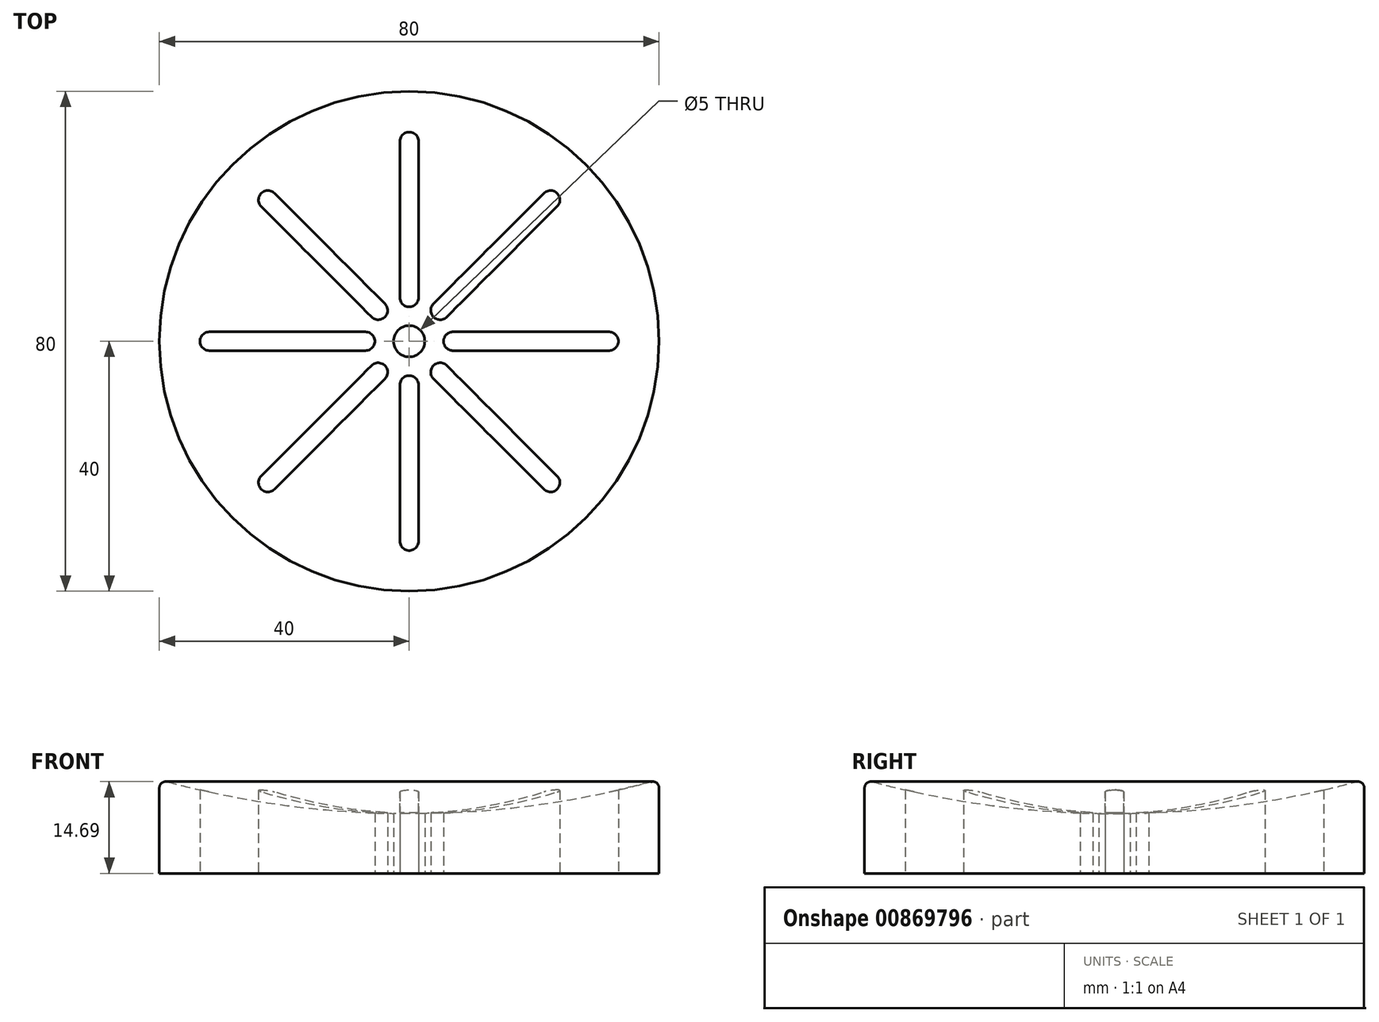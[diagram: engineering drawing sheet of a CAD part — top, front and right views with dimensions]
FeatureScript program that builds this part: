
annotation { "Feature Type Name" : "Feature", "Feature Type Description" : "" }
export const myFeature = defineFeature(function(context is Context, id is Id, definition is map)
    precondition{}
    {
        {
            var Q0;
            Q0=qCreatedBy(makeId("Top.planeOp"),FACE);
            var sketch = newSketch(context, id + "F0", { "sketchPlane" : qUnion([Q0])});
            skCircle(sketch, "E0", {"center": v(0, 0) * mm, "radius": 40 * mm});
            skSolve(sketch);
        }
        {
            var Q0;
            Q0=makeQuery(id+"F0.imprint","IMPRINT",FACE,{"disambiguationData":[TD([[makeQuery(id+"F0.imprint","IMPRINT",EDGE,{"derivedFrom":sQuery(id+"F0.wireOp",EDGE,"E0")}),1.0]])]});
            extrude(context, id + "F1", {"entities" : qUnion([Q0]), "depth" : 15 * mm, "offsetDistance" : 25 * mm});
        }
        {
            var Q0;
            Q0=qCreatedBy(makeId("Front.planeOp"),FACE);
            var sketch = newSketch(context, id + "F2", { "sketchPlane" : qUnion([Q0])});
            skArc(sketch, "E1", {"start": v(0, 9.57) * mm, "mid": v(20.18, 10.93) * mm, "end": v(40, 15) * mm});
            skLineSegment(sketch, "E2.0.0", {"start": v(0, 15) * mm, "end": v(40, 15) * mm});
            skLineSegment(sketch, "E3", {"start": v(0, 15) * mm, "end": v(0, 9.57) * mm});
            skPoint(sketch, "E4.orphan", {"position": v(-40, 15) * mm});
            skSolve(sketch);
        }
        {
            var Q0;
            Q0 = qSketchRegion(id + "F2", true);
            var Q1;
            Q1=sQuery(id+"F2.wireOp",EDGE,"E3");
            revolve(context, id + "F3", {"operationType" : NewBodyOperationType.REMOVE, "surfaceOperationType" : NewSurfaceOperationType.NEW, "entities" : qUnion([Q0]), "axis" : qUnion([Q1]), "revolveType" : RevolveType.FULL, "oppositeDirection" : true});
        }
        {
            var Q0;
            Q0=makeQuery(id+"F3.boolean.opBoolean","MERGE",EDGE,{"derivedFrom":[makeQuery(id+"F1.opExtrude","CAP_EDGE",EDGE,{"disambiguationData":[OSD([sQuery(id+"F0.wireOp",EDGE,"E0")])],"isStart":false}),makeQuery(id+"F3.opRevolve","SWEPT_EDGE",EDGE,{"disambiguationData":[OSD([sQuery(id+"F2.wireOp",EDGE,"E1"),sQuery(id+"F2.wireOp",EDGE,"E2.0.0")])]})]});
            fillet(context, id + "F4", {"entities" : qUnion([Q0]), "radius" : 1 * mm, "tangentPropagation" : true, "allowEdgeOverflow" : false});
        }
        {
            var Q0;
            Q0=qCreatedBy(makeId("Top.planeOp"),FACE);
            var sketch = newSketch(context, id + "F5", { "sketchPlane" : qUnion([Q0])});
            skCircle(sketch, "E5", {"center": v(0, 0) * mm, "radius": 2.5 * mm});
            skArc(sketch, "E6", {"start": v(-1.5, 7) * mm, "mid": v(0, 5.5) * mm, "end": v(1.5, 7) * mm});
            skArc(sketch, "E7", {"start": v(1.5, 32) * mm, "mid": v(0, 33.5) * mm, "end": v(-1.5, 32) * mm});
            skLineSegment(sketch, "E8", {"start": v(-1.5, 32) * mm, "end": v(-1.5, 7) * mm});
            skLineSegment(sketch, "E9", {"start": v(1.5, 32) * mm, "end": v(1.5, 7) * mm});
            skArc(sketch, "E10.1.0", {"start": v(-21.57, 23.69) * mm, "mid": v(-23.69, 23.69) * mm, "end": v(-23.69, 21.57) * mm});
            skLineSegment(sketch, "E10.1.1", {"start": v(-23.69, 21.57) * mm, "end": v(-6.01, 3.89) * mm});
            skLineSegment(sketch, "E10.1.2", {"start": v(-21.57, 23.69) * mm, "end": v(-3.89, 6.01) * mm});
            skArc(sketch, "E10.1.3", {"start": v(-6.01, 3.89) * mm, "mid": v(-3.89, 3.89) * mm, "end": v(-3.89, 6.01) * mm});
            skArc(sketch, "E10.2.0", {"start": v(-32, 1.5) * mm, "mid": v(-33.5, 0) * mm, "end": v(-32, -1.5) * mm});
            skLineSegment(sketch, "E10.2.1", {"start": v(-32, -1.5) * mm, "end": v(-7, -1.5) * mm});
            skLineSegment(sketch, "E10.2.2", {"start": v(-32, 1.5) * mm, "end": v(-7, 1.5) * mm});
            skArc(sketch, "E10.2.3", {"start": v(-7, -1.5) * mm, "mid": v(-5.5, 0) * mm, "end": v(-7, 1.5) * mm});
            skArc(sketch, "E10.3.0", {"start": v(-23.69, -21.57) * mm, "mid": v(-23.69, -23.69) * mm, "end": v(-21.57, -23.69) * mm});
            skLineSegment(sketch, "E10.3.1", {"start": v(-21.57, -23.69) * mm, "end": v(-3.89, -6.01) * mm});
            skLineSegment(sketch, "E10.3.2", {"start": v(-23.69, -21.57) * mm, "end": v(-6.01, -3.89) * mm});
            skArc(sketch, "E10.3.3", {"start": v(-3.89, -6.01) * mm, "mid": v(-3.89, -3.89) * mm, "end": v(-6.01, -3.89) * mm});
            skArc(sketch, "E10.4.0", {"start": v(-1.5, -32) * mm, "mid": v(0, -33.5) * mm, "end": v(1.5, -32) * mm});
            skLineSegment(sketch, "E10.4.1", {"start": v(1.5, -32) * mm, "end": v(1.5, -7) * mm});
            skLineSegment(sketch, "E10.4.2", {"start": v(-1.5, -32) * mm, "end": v(-1.5, -7) * mm});
            skArc(sketch, "E10.4.3", {"start": v(1.5, -7) * mm, "mid": v(0, -5.5) * mm, "end": v(-1.5, -7) * mm});
            skArc(sketch, "E10.5.0", {"start": v(21.57, -23.69) * mm, "mid": v(23.69, -23.69) * mm, "end": v(23.69, -21.57) * mm});
            skLineSegment(sketch, "E10.5.1", {"start": v(23.69, -21.57) * mm, "end": v(6.01, -3.89) * mm});
            skLineSegment(sketch, "E10.5.2", {"start": v(21.57, -23.69) * mm, "end": v(3.89, -6.01) * mm});
            skArc(sketch, "E10.5.3", {"start": v(6.01, -3.89) * mm, "mid": v(3.89, -3.89) * mm, "end": v(3.89, -6.01) * mm});
            skArc(sketch, "E10.6.0", {"start": v(32, -1.5) * mm, "mid": v(33.5, 0) * mm, "end": v(32, 1.5) * mm});
            skLineSegment(sketch, "E10.6.1", {"start": v(32, 1.5) * mm, "end": v(7, 1.5) * mm});
            skLineSegment(sketch, "E10.6.2", {"start": v(32, -1.5) * mm, "end": v(7, -1.5) * mm});
            skArc(sketch, "E10.6.3", {"start": v(7, 1.5) * mm, "mid": v(5.5, 0) * mm, "end": v(7, -1.5) * mm});
            skArc(sketch, "E10.7.0", {"start": v(23.69, 21.57) * mm, "mid": v(23.69, 23.69) * mm, "end": v(21.57, 23.69) * mm});
            skLineSegment(sketch, "E10.7.1", {"start": v(21.57, 23.69) * mm, "end": v(3.89, 6.01) * mm});
            skLineSegment(sketch, "E10.7.2", {"start": v(23.69, 21.57) * mm, "end": v(6.01, 3.89) * mm});
            skArc(sketch, "E10.7.3", {"start": v(3.89, 6.01) * mm, "mid": v(3.89, 3.89) * mm, "end": v(6.01, 3.89) * mm});
            skSolve(sketch);
        }
        {
            var Q0;
            Q0 = qSketchRegion(id + "F5", true);
            extrude(context, id + "F6", {"entities" : qUnion([Q0]), "operationType" : NewBodyOperationType.REMOVE, "depth" : 25 * mm, "offsetDistance" : 25 * mm});
        }
    });
